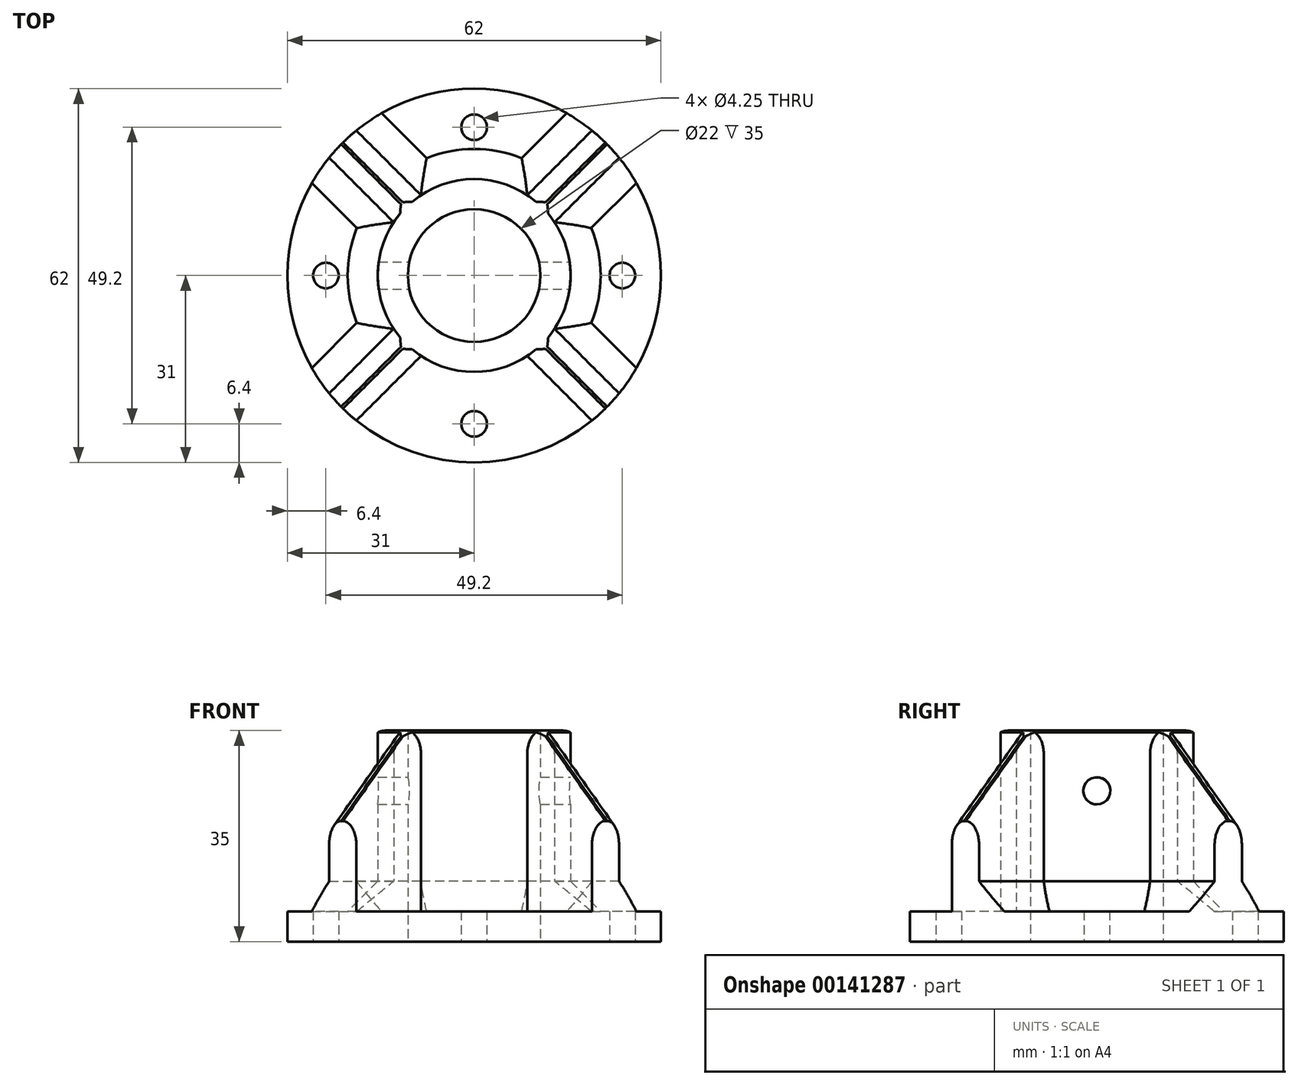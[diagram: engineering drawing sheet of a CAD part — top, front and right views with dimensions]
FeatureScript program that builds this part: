
annotation { "Feature Type Name" : "Feature", "Feature Type Description" : "" }
export const myFeature = defineFeature(function(context is Context, id is Id, definition is map)
    precondition{}
    {
        {
            var Q0;
            Q0=qCreatedBy(makeId("Top.planeOp"),FACE);
            var sketch = newSketch(context, id + "F0", { "sketchPlane" : qUnion([Q0])});
            skCircle(sketch, "E0", {"center": v(0, 0) * mm, "radius": 11 * mm});
            skCircle(sketch, "E1", {"center": v(0, 0) * mm, "radius": 31 * mm});
            skCircle(sketch, "E2", {"center": v(24.6, 0) * mm, "radius": 2.12 * mm});
            skCircle(sketch, "E3.1.0", {"center": v(0, 24.6) * mm, "radius": 2.12 * mm});
            skCircle(sketch, "E3.2.0", {"center": v(-24.6, 0) * mm, "radius": 2.12 * mm});
            skCircle(sketch, "E3.3.0", {"center": v(0, -24.6) * mm, "radius": 2.12 * mm});
            skSolve(sketch);
        }
        {
            var Q0;
            Q0 = qSketchRegion(id + "F0", true);
            extrude(context, id + "F1", {"entities" : qUnion([Q0]), "depth" : 5 * mm});
        }
        {
            var Q0;
            Q0=makeQuery(id+"F1.opExtrude","CAP_FACE",FACE,{"disambiguationData":[OSD([sQuery(id+"F0.wireOp",EDGE,"E0"),sQuery(id+"F0.wireOp",EDGE,"E1")])],"isStart":false});
            var sketch = newSketch(context, id + "F2", { "sketchPlane" : qUnion([Q0])});
            skArc(sketch, "E4", {"start": v(-13.35, 8.83) * mm, "mid": v(-16, 0) * mm, "end": v(-13.35, -8.83) * mm});
            skCircle(sketch, "E5", {"center": v(0, 0) * mm, "radius": 11 * mm});
            skLineSegment(sketch, "E6", {"start": v(0, 0) * mm, "end": v(21.92, 21.92) * mm, "construction": true});
            skArc(sketch, "E7", {"start": v(19.54, 24.06) * mm, "mid": v(20.76, 23.02) * mm, "end": v(21.92, 21.92) * mm});
            skLineSegment(sketch, "E8", {"start": v(8.83, 13.35) * mm, "end": v(19.54, 24.06) * mm});
            skArc(sketch, "E9.MirrorCS", {"start": v(24.06, 19.54) * mm, "mid": v(23.02, 20.76) * mm, "end": v(21.92, 21.92) * mm});
            skLineSegment(sketch, "E10.MirrorCS", {"start": v(13.35, 8.83) * mm, "end": v(24.06, 19.54) * mm});
            skLineSegment(sketch, "E11.1.0", {"start": v(-13.35, 8.83) * mm, "end": v(-24.06, 19.54) * mm});
            skArc(sketch, "E11.1.1", {"start": v(-24.06, 19.54) * mm, "mid": v(-23.02, 20.76) * mm, "end": v(-21.92, 21.92) * mm});
            skArc(sketch, "E11.1.2", {"start": v(-19.54, 24.06) * mm, "mid": v(-20.76, 23.02) * mm, "end": v(-21.92, 21.92) * mm});
            skLineSegment(sketch, "E11.1.3", {"start": v(-8.83, 13.35) * mm, "end": v(-19.54, 24.06) * mm});
            skLineSegment(sketch, "E11.2.0", {"start": v(-8.83, -13.35) * mm, "end": v(-19.54, -24.06) * mm});
            skArc(sketch, "E11.2.1", {"start": v(-19.54, -24.06) * mm, "mid": v(-20.76, -23.02) * mm, "end": v(-21.92, -21.92) * mm});
            skArc(sketch, "E11.2.2", {"start": v(-24.06, -19.54) * mm, "mid": v(-23.02, -20.76) * mm, "end": v(-21.92, -21.92) * mm});
            skLineSegment(sketch, "E11.2.3", {"start": v(-13.35, -8.83) * mm, "end": v(-24.06, -19.54) * mm});
            skLineSegment(sketch, "E11.3.0", {"start": v(13.35, -8.83) * mm, "end": v(24.06, -19.54) * mm});
            skArc(sketch, "E11.3.1", {"start": v(24.06, -19.54) * mm, "mid": v(23.02, -20.76) * mm, "end": v(21.92, -21.92) * mm});
            skArc(sketch, "E11.3.2", {"start": v(19.54, -24.06) * mm, "mid": v(20.76, -23.02) * mm, "end": v(21.92, -21.92) * mm});
            skLineSegment(sketch, "E11.3.3", {"start": v(8.83, -13.35) * mm, "end": v(19.54, -24.06) * mm});
            skArc(sketch, "E12.trimOffspring", {"start": v(-8.83, -13.35) * mm, "mid": v(0, -16) * mm, "end": v(8.83, -13.35) * mm});
            skArc(sketch, "E13.trimOffspring", {"start": v(8.83, 13.35) * mm, "mid": v(0, 16) * mm, "end": v(-8.83, 13.35) * mm});
            skArc(sketch, "E14.trimOffspring", {"start": v(13.35, -8.83) * mm, "mid": v(16, 0) * mm, "end": v(13.35, 8.83) * mm});
            skSolve(sketch);
        }
        {
            var Q0;
            Q0 = qSketchRegion(id + "F2", true);
            extrude(context, id + "F3", {"entities" : qUnion([Q0]), "operationType" : NewBodyOperationType.ADD, "depth" : 30 * mm});
        }
        {
            var Q0;
            Q0=makeQuery(id+"F3.opExtrude","CAP_EDGE",EDGE,{"disambiguationData":[OSD([sQuery(id+"F2.wireOp",EDGE,"E11.2.1"),sQuery(id+"F2.wireOp",EDGE,"E11.2.2")])],"isStart":false});
            var Q1;
            Q1=makeQuery(id+"F3.opExtrude","CAP_EDGE",EDGE,{"disambiguationData":[OSD([sQuery(id+"F2.wireOp",EDGE,"E11.3.1"),sQuery(id+"F2.wireOp",EDGE,"E11.3.2")])],"isStart":false});
            var Q2;
            Q2=makeQuery(id+"F3.opExtrude","CAP_EDGE",EDGE,{"disambiguationData":[OSD([sQuery(id+"F2.wireOp",EDGE,"E7"),sQuery(id+"F2.wireOp",EDGE,"E9.MirrorCS")])],"isStart":false});
            var Q3;
            Q3=makeQuery(id+"F3.opExtrude","CAP_EDGE",EDGE,{"disambiguationData":[OSD([sQuery(id+"F2.wireOp",EDGE,"E11.1.1"),sQuery(id+"F2.wireOp",EDGE,"E11.1.2")])],"isStart":false});
            chamfer(context, id + "F4", {"entities" : qUnion([Q0, Q1, Q2, Q3]), "width" : 15 * mm, "tangentPropagation" : true});
        }
        {
            var Q0;
            Q0=makeQuery(id+"F3.opExtrude","CAP_EDGE",EDGE,{"disambiguationData":[OSD([sQuery(id+"F2.wireOp",EDGE,"E12.trimOffspring")])],"isStart":true});
            var Q1;
            Q1=makeQuery(id+"F3.opExtrude","CAP_EDGE",EDGE,{"disambiguationData":[OSD([sQuery(id+"F2.wireOp",EDGE,"E11.3.3")])],"isStart":true});
            var Q2;
            Q2=makeQuery(id+"F3.opExtrude","CAP_EDGE",EDGE,{"disambiguationData":[OSD([sQuery(id+"F2.wireOp",EDGE,"E11.2.0")])],"isStart":true});
            var Q3;
            Q3=makeQuery(id+"F3.opExtrude","CAP_EDGE",EDGE,{"disambiguationData":[OSD([sQuery(id+"F2.wireOp",EDGE,"E14.trimOffspring")])],"isStart":true});
            var Q4;
            Q4=makeQuery(id+"F3.opExtrude","CAP_EDGE",EDGE,{"disambiguationData":[OSD([sQuery(id+"F2.wireOp",EDGE,"E10.MirrorCS")])],"isStart":true});
            var Q5;
            Q5=makeQuery(id+"F3.opExtrude","CAP_EDGE",EDGE,{"disambiguationData":[OSD([sQuery(id+"F2.wireOp",EDGE,"E11.3.0")])],"isStart":true});
            var Q6;
            Q6=makeQuery(id+"F3.opExtrude","CAP_EDGE",EDGE,{"disambiguationData":[OSD([sQuery(id+"F2.wireOp",EDGE,"E13.trimOffspring")])],"isStart":true});
            var Q7;
            Q7=makeQuery(id+"F3.opExtrude","CAP_EDGE",EDGE,{"disambiguationData":[OSD([sQuery(id+"F2.wireOp",EDGE,"E11.1.3")])],"isStart":true});
            var Q8;
            Q8=makeQuery(id+"F3.opExtrude","CAP_EDGE",EDGE,{"disambiguationData":[OSD([sQuery(id+"F2.wireOp",EDGE,"E8")])],"isStart":true});
            var Q9;
            Q9=makeQuery(id+"F3.opExtrude","CAP_EDGE",EDGE,{"disambiguationData":[OSD([sQuery(id+"F2.wireOp",EDGE,"E4")])],"isStart":true});
            var Q10;
            Q10=makeQuery(id+"F3.opExtrude","CAP_EDGE",EDGE,{"disambiguationData":[OSD([sQuery(id+"F2.wireOp",EDGE,"E11.1.0")])],"isStart":true});
            var Q11;
            Q11=makeQuery(id+"F3.opExtrude","CAP_EDGE",EDGE,{"disambiguationData":[OSD([sQuery(id+"F2.wireOp",EDGE,"E11.2.3")])],"isStart":true});
            chamfer(context, id + "F5", {"entities" : qUnion([Q0, Q1, Q2, Q3, Q4, Q5, Q6, Q7, Q8, Q9, Q10, Q11]), "width" : 5 * mm, "tangentPropagation" : true});
        }
        {
            var Q0;
            Q0=makeQuery(id+"F4.opChamfer","BLEND_EDGE",EDGE,{"blendedFrom":[makeQuery(id+"F3.opExtrude","CAP_EDGE",EDGE,{"disambiguationData":[OSD([sQuery(id+"F2.wireOp",EDGE,"E11.2.1"),sQuery(id+"F2.wireOp",EDGE,"E11.2.2")])],"isStart":false}),makeQuery(id+"F3.opExtrude","SWEPT_FACE",FACE,{"disambiguationData":[OSD([sQuery(id+"F2.wireOp",EDGE,"E11.2.3")])]})],"blendedInto":[makeQuery(id+"F3.opExtrude","SWEPT_FACE",FACE,{"disambiguationData":[OSD([sQuery(id+"F2.wireOp",EDGE,"E11.2.3")])]})]});
            var Q1;
            Q1=makeQuery(id+"F4.opChamfer","BLEND_EDGE",EDGE,{"blendedFrom":[makeQuery(id+"F3.opExtrude","CAP_EDGE",EDGE,{"disambiguationData":[OSD([sQuery(id+"F2.wireOp",EDGE,"E11.2.1"),sQuery(id+"F2.wireOp",EDGE,"E11.2.2")])],"isStart":false}),makeQuery(id+"F3.opExtrude","SWEPT_FACE",FACE,{"disambiguationData":[OSD([sQuery(id+"F2.wireOp",EDGE,"E11.2.0")])]})],"blendedInto":[makeQuery(id+"F3.opExtrude","SWEPT_FACE",FACE,{"disambiguationData":[OSD([sQuery(id+"F2.wireOp",EDGE,"E11.2.0")])]})]});
            var Q2;
            Q2=makeQuery(id+"F4.opChamfer","BLEND_EDGE",EDGE,{"blendedFrom":[makeQuery(id+"F3.opExtrude","CAP_EDGE",EDGE,{"disambiguationData":[OSD([sQuery(id+"F2.wireOp",EDGE,"E11.3.1"),sQuery(id+"F2.wireOp",EDGE,"E11.3.2")])],"isStart":false}),makeQuery(id+"F3.opExtrude","SWEPT_FACE",FACE,{"disambiguationData":[OSD([sQuery(id+"F2.wireOp",EDGE,"E11.3.3")])]})],"blendedInto":[makeQuery(id+"F3.opExtrude","SWEPT_FACE",FACE,{"disambiguationData":[OSD([sQuery(id+"F2.wireOp",EDGE,"E11.3.3")])]})]});
            var Q3;
            Q3=makeQuery(id+"F4.opChamfer","BLEND_EDGE",EDGE,{"blendedFrom":[makeQuery(id+"F3.opExtrude","CAP_EDGE",EDGE,{"disambiguationData":[OSD([sQuery(id+"F2.wireOp",EDGE,"E11.3.1"),sQuery(id+"F2.wireOp",EDGE,"E11.3.2")])],"isStart":false}),makeQuery(id+"F3.opExtrude","SWEPT_FACE",FACE,{"disambiguationData":[OSD([sQuery(id+"F2.wireOp",EDGE,"E11.3.0")])]})],"blendedInto":[makeQuery(id+"F3.opExtrude","SWEPT_FACE",FACE,{"disambiguationData":[OSD([sQuery(id+"F2.wireOp",EDGE,"E11.3.0")])]})]});
            var Q4;
            Q4=makeQuery(id+"F4.opChamfer","BLEND_EDGE",EDGE,{"blendedFrom":[makeQuery(id+"F3.opExtrude","CAP_EDGE",EDGE,{"disambiguationData":[OSD([sQuery(id+"F2.wireOp",EDGE,"E7"),sQuery(id+"F2.wireOp",EDGE,"E9.MirrorCS")])],"isStart":false}),makeQuery(id+"F3.opExtrude","SWEPT_FACE",FACE,{"disambiguationData":[OSD([sQuery(id+"F2.wireOp",EDGE,"E10.MirrorCS")])]})],"blendedInto":[makeQuery(id+"F3.opExtrude","SWEPT_FACE",FACE,{"disambiguationData":[OSD([sQuery(id+"F2.wireOp",EDGE,"E10.MirrorCS")])]})]});
            var Q5;
            Q5=makeQuery(id+"F4.opChamfer","BLEND_EDGE",EDGE,{"blendedFrom":[makeQuery(id+"F3.opExtrude","CAP_EDGE",EDGE,{"disambiguationData":[OSD([sQuery(id+"F2.wireOp",EDGE,"E7"),sQuery(id+"F2.wireOp",EDGE,"E9.MirrorCS")])],"isStart":false}),makeQuery(id+"F3.opExtrude","SWEPT_FACE",FACE,{"disambiguationData":[OSD([sQuery(id+"F2.wireOp",EDGE,"E8")])]})],"blendedInto":[makeQuery(id+"F3.opExtrude","SWEPT_FACE",FACE,{"disambiguationData":[OSD([sQuery(id+"F2.wireOp",EDGE,"E8")])]})]});
            var Q6;
            Q6=makeQuery(id+"F4.opChamfer","BLEND_EDGE",EDGE,{"blendedFrom":[makeQuery(id+"F3.opExtrude","CAP_EDGE",EDGE,{"disambiguationData":[OSD([sQuery(id+"F2.wireOp",EDGE,"E11.1.1"),sQuery(id+"F2.wireOp",EDGE,"E11.1.2")])],"isStart":false}),makeQuery(id+"F3.opExtrude","SWEPT_FACE",FACE,{"disambiguationData":[OSD([sQuery(id+"F2.wireOp",EDGE,"E11.1.3")])]})],"blendedInto":[makeQuery(id+"F3.opExtrude","SWEPT_FACE",FACE,{"disambiguationData":[OSD([sQuery(id+"F2.wireOp",EDGE,"E11.1.3")])]})]});
            var Q7;
            Q7=makeQuery(id+"F4.opChamfer","BLEND_EDGE",EDGE,{"blendedFrom":[makeQuery(id+"F3.opExtrude","CAP_EDGE",EDGE,{"disambiguationData":[OSD([sQuery(id+"F2.wireOp",EDGE,"E11.1.1"),sQuery(id+"F2.wireOp",EDGE,"E11.1.2")])],"isStart":false}),makeQuery(id+"F3.opExtrude","SWEPT_FACE",FACE,{"disambiguationData":[OSD([sQuery(id+"F2.wireOp",EDGE,"E11.1.0")])]})],"blendedInto":[makeQuery(id+"F3.opExtrude","SWEPT_FACE",FACE,{"disambiguationData":[OSD([sQuery(id+"F2.wireOp",EDGE,"E11.1.0")])]})]});
            fillet(context, id + "F6", {"entities" : qUnion([Q0, Q1, Q2, Q3, Q4, Q5, Q6, Q7]), "radius" : 3 * mm, "tangentPropagation" : true, "allowEdgeOverflow" : false});
        }
        {
            var Q0;
            Q0=makeQuery(id+"F3.opExtrude","CAP_EDGE",EDGE,{"disambiguationData":[OSD([sQuery(id+"F2.wireOp",EDGE,"E12.trimOffspring")])],"isStart":false});
            var Q1;
            Q1=makeQuery(id+"F3.opExtrude","CAP_EDGE",EDGE,{"disambiguationData":[OSD([sQuery(id+"F2.wireOp",EDGE,"E14.trimOffspring")])],"isStart":false});
            var Q2;
            Q2=makeQuery(id+"F3.opExtrude","CAP_EDGE",EDGE,{"disambiguationData":[OSD([sQuery(id+"F2.wireOp",EDGE,"E13.trimOffspring")])],"isStart":false});
            var Q3;
            Q3=makeQuery(id+"F3.opExtrude","CAP_EDGE",EDGE,{"disambiguationData":[OSD([sQuery(id+"F2.wireOp",EDGE,"E4")])],"isStart":false});
            fillet(context, id + "F7", {"entities" : qUnion([Q0, Q1, Q2, Q3]), "radius" : 3.2 * mm, "tangentPropagation" : true, "allowEdgeOverflow" : false});
        }
        {
            var Q0;
            Q0=qCreatedBy(makeId("Right.planeOp"),FACE);
            var sketch = newSketch(context, id + "F8", { "sketchPlane" : qUnion([Q0])});
            skCircle(sketch, "E15", {"center": v(0, 25) * mm, "radius": 2.25 * mm});
            skSolve(sketch);
        }
        {
            var Q0;
            Q0 = qSketchRegion(id + "F8", true);
            extrude(context, id + "F9", {"entities" : qUnion([Q0]), "operationType" : NewBodyOperationType.REMOVE, "endBound" : BoundingType.SYMMETRIC, "oppositeDirection" : true, "depth" : 35 * mm});
        }
    });
